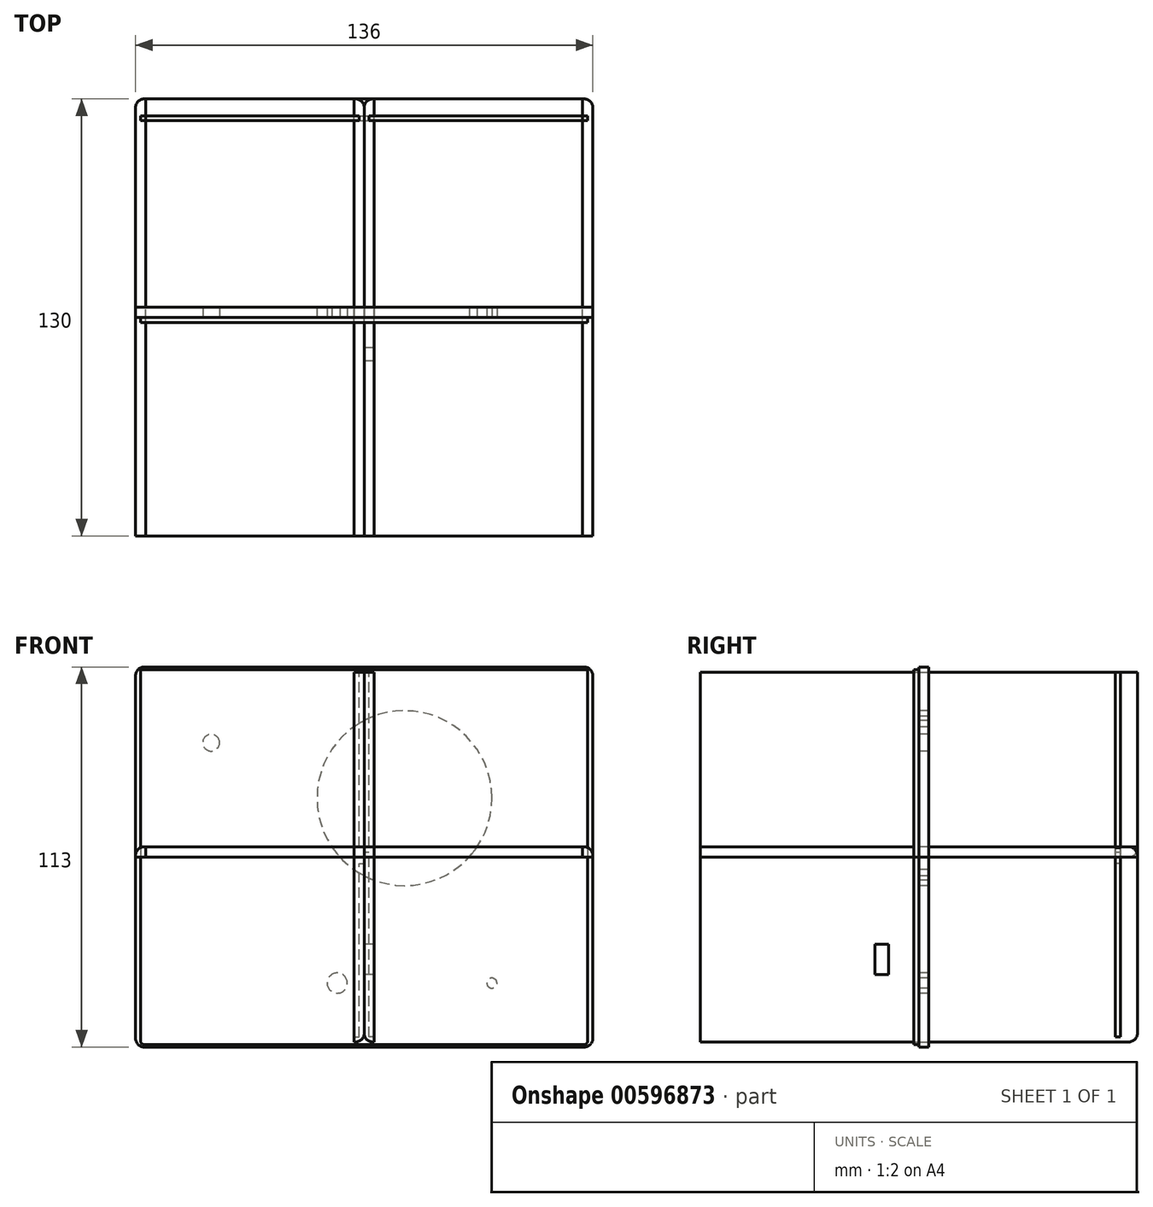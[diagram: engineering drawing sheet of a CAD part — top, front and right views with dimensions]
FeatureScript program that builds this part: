
annotation { "Feature Type Name" : "Feature", "Feature Type Description" : "" }
export const myFeature = defineFeature(function(context is Context, id is Id, definition is map)
    precondition{}
    {
        {
            var Q0;
            Q0=qCreatedBy(makeId("Right.planeOp"),FACE);
            var sketch = newSketch(context, id + "F0", { "sketchPlane" : qUnion([Q0])});
            skLineSegment(sketch, "E0.bottom", {"start": v(-65, 55) * mm, "end": v(65, 55) * mm});
            skLineSegment(sketch, "E0.top", {"start": v(-65, -55) * mm, "end": v(65, -55) * mm});
            skLineSegment(sketch, "E0.left", {"start": v(-65, 55) * mm, "end": v(-65, -55) * mm});
            skLineSegment(sketch, "E0.right", {"start": v(65, 55) * mm, "end": v(65, -55) * mm});
            skPoint(sketch, "E0.middle", {"position": v(0, 0) * mm});
            skSolve(sketch);
        }
        {
            var Q0;
            Q0 = qSketchRegion(id + "F0", true);
            extrude(context, id + "F1", {"entities" : qUnion([Q0]), "oppositeDirection" : true, "depth" : 3 * mm, "offsetDistance" : 25.4 * mm});
        }
        {
            var Q0;
            Q0=makeQuery(id+"F1.opExtrude","SWEPT_FACE",FACE,{"disambiguationData":[OSD([sQuery(id+"F0.wireOp",EDGE,"E0.bottom")])]});
            var sketch = newSketch(context, id + "F2", { "sketchPlane" : qUnion([Q0])});
            skLineSegment(sketch, "E1.bottom", {"start": v(-3, 60) * mm, "end": v(-1.5, 60) * mm});
            skLineSegment(sketch, "E1.top", {"start": v(-3, 58.5) * mm, "end": v(-1.5, 58.5) * mm});
            skLineSegment(sketch, "E1.left", {"start": v(-3, 60) * mm, "end": v(-3, 58.5) * mm});
            skLineSegment(sketch, "E1.right", {"start": v(-1.5, 60) * mm, "end": v(-1.5, 58.5) * mm});
            skSolve(sketch);
        }
        {
            var Q0;
            Q0 = qSketchRegion(id + "F2", true);
            extrude(context, id + "F3", {"entities" : qUnion([Q0]), "operationType" : NewBodyOperationType.REMOVE, "oppositeDirection" : true, "depth" : 108.5 * mm, "offsetDistance" : 25.4 * mm});
        }
        {
            var Q0;
            Q0=qCreatedBy(makeId("Top.planeOp"),FACE);
            var sketch = newSketch(context, id + "F4", { "sketchPlane" : qUnion([Q0])});
            skLineSegment(sketch, "E2.bottom", {"start": v(-68, 65) * mm, "end": v(68, 65) * mm});
            skLineSegment(sketch, "E2.top", {"start": v(-68, -65) * mm, "end": v(68, -65) * mm});
            skLineSegment(sketch, "E2.left", {"start": v(-68, 65) * mm, "end": v(-68, -65) * mm});
            skLineSegment(sketch, "E2.right", {"start": v(68, 65) * mm, "end": v(68, -65) * mm});
            skPoint(sketch, "E2.middle", {"position": v(0, 0) * mm});
            skSolve(sketch);
        }
        {
            var Q0;
            Q0 = qSketchRegion(id + "F4", true);
            extrude(context, id + "F5", {"entities" : qUnion([Q0]), "depth" : 3 * mm, "offsetDistance" : 25.4 * mm});
        }
        {
            var Q0;
            Q0=makeQuery(id+"F5.opExtrude","CAP_FACE",FACE,{"disambiguationData":[OSD([sQuery(id+"F4.wireOp",EDGE,"E2.bottom"),sQuery(id+"F4.wireOp",EDGE,"E2.top"),sQuery(id+"F4.wireOp",EDGE,"E2.left"),sQuery(id+"F4.wireOp",EDGE,"E2.right")])],"isStart":false});
            var sketch = newSketch(context, id + "F6", { "sketchPlane" : qUnion([Q0])});
            skLineSegment(sketch, "E3.bottom", {"start": v(-66.5, 58.5) * mm, "end": v(66.5, 58.5) * mm});
            skLineSegment(sketch, "E3.top", {"start": v(-66.5, 60) * mm, "end": v(66.5, 60) * mm});
            skLineSegment(sketch, "E3.left", {"start": v(-66.5, 58.5) * mm, "end": v(-66.5, 60) * mm});
            skLineSegment(sketch, "E3.right", {"start": v(66.5, 58.5) * mm, "end": v(66.5, 60) * mm});
            skPoint(sketch, "E3.middle", {"position": v(0, 59.25) * mm});
            skSolve(sketch);
        }
        {
            var Q0;
            Q0=makeQuery(id+"F6.imprint","IMPRINT",FACE,{"disambiguationData":[TD([[makeQuery(id+"F6.imprint","IMPRINT",EDGE,{"derivedFrom":sQuery(id+"F6.wireOp",EDGE,"E3.bottom")}),1.0]])]});
            var Q1;
            Q1 = qSketchRegion(id + "F6", true);
            extrude(context, id + "F7", {"entities" : qUnion([Q0, Q1]), "operationType" : NewBodyOperationType.REMOVE, "oppositeDirection" : true, "depth" : 5 * mm, "offsetDistance" : 25.4 * mm});
        }
        {
            var Q0;
            Q0=qCreatedBy(makeId("Front.planeOp"),FACE);
            var sketch = newSketch(context, id + "F8", { "sketchPlane" : qUnion([Q0])});
            skLineSegment(sketch, "E4.bottom", {"start": v(66.5, 55.75) * mm, "end": v(-66.5, 55.75) * mm});
            skLineSegment(sketch, "E4.top", {"start": v(66.5, -55.75) * mm, "end": v(-66.5, -55.75) * mm});
            skLineSegment(sketch, "E4.left", {"start": v(66.5, 55.75) * mm, "end": v(66.5, -55.75) * mm});
            skLineSegment(sketch, "E4.right", {"start": v(-66.5, 55.75) * mm, "end": v(-66.5, -55.75) * mm});
            skPoint(sketch, "E4.middle", {"position": v(0, 0) * mm});
            skSolve(sketch);
        }
        {
            var Q0;
            Q0 = qSketchRegion(id + "F8", true);
            extrude(context, id + "F9", {"entities" : qUnion([Q0]), "depth" : 1.5 * mm, "offsetDistance" : 25.4 * mm});
        }
        {
            var Q0;
            Q0 = qSketchRegion(id + "F0", true);
            extrude(context, id + "F10", {"entities" : qUnion([Q0]), "depth" : 3 * mm, "offsetDistance" : 25.4 * mm});
        }
        {
            var Q0;
            Q0=makeQuery(id+"F10.opExtrude","SWEPT_FACE",FACE,{"disambiguationData":[OSD([sQuery(id+"F0.wireOp",EDGE,"E0.bottom")])]});
            var sketch = newSketch(context, id + "F11", { "sketchPlane" : qUnion([Q0])});
            skLineSegment(sketch, "E5.bottom", {"start": v(3, 60) * mm, "end": v(1.5, 60) * mm});
            skLineSegment(sketch, "E5.top", {"start": v(3, 58.5) * mm, "end": v(1.5, 58.5) * mm});
            skLineSegment(sketch, "E5.left", {"start": v(3, 60) * mm, "end": v(3, 58.5) * mm});
            skLineSegment(sketch, "E5.right", {"start": v(1.5, 60) * mm, "end": v(1.5, 58.5) * mm});
            skSolve(sketch);
        }
        {
            var Q0;
            Q0 = qSketchRegion(id + "F11", true);
            extrude(context, id + "F12", {"entities" : qUnion([Q0]), "operationType" : NewBodyOperationType.REMOVE, "oppositeDirection" : true, "depth" : 108.5 * mm, "offsetDistance" : 25.4 * mm});
        }
        {
            var Q0;
            Q0=qCreatedBy(makeId("Top.planeOp"),FACE);
            var sketch = newSketch(context, id + "F13", { "sketchPlane" : qUnion([Q0])});
            skLineSegment(sketch, "E6.bottom", {"start": v(-65, -65) * mm, "end": v(65, -65) * mm});
            skLineSegment(sketch, "E6.top", {"start": v(-65, 65) * mm, "end": v(65, 65) * mm});
            skLineSegment(sketch, "E6.left", {"start": v(-65, -65) * mm, "end": v(-65, 65) * mm});
            skLineSegment(sketch, "E6.right", {"start": v(65, -65) * mm, "end": v(65, 65) * mm});
            skPoint(sketch, "E6.middle", {"position": v(0, 0) * mm});
            skSolve(sketch);
        }
        {
            var Q0;
            Q0 = qSketchRegion(id + "F13", true);
            extrude(context, id + "F14", {"entities" : qUnion([Q0]), "depth" : 3 * mm, "offsetDistance" : 25.4 * mm});
        }
        {
            var Q0;
            Q0=makeQuery(id+"F10.opExtrude","CAP_FACE",FACE,{"disambiguationData":[OSD([sQuery(id+"F0.wireOp",EDGE,"E0.bottom"),sQuery(id+"F0.wireOp",EDGE,"E0.top"),sQuery(id+"F0.wireOp",EDGE,"E0.left"),sQuery(id+"F0.wireOp",EDGE,"E0.right")])],"isStart":true});
            var sketch = newSketch(context, id + "F15", { "sketchPlane" : qUnion([Q0])});
            skLineSegment(sketch, "E7.bottom", {"start": v(9, -26) * mm, "end": v(13, -26) * mm});
            skLineSegment(sketch, "E7.top", {"start": v(9, -35) * mm, "end": v(13, -35) * mm});
            skLineSegment(sketch, "E7.left", {"start": v(9, -26) * mm, "end": v(9, -35) * mm});
            skLineSegment(sketch, "E7.right", {"start": v(13, -26) * mm, "end": v(13, -35) * mm});
            skSolve(sketch);
        }
        {
            var Q0;
            Q0 = qSketchRegion(id + "F15", true);
            extrude(context, id + "F16", {"entities" : qUnion([Q0]), "operationType" : NewBodyOperationType.REMOVE, "oppositeDirection" : true, "depth" : 3 * mm, "offsetDistance" : 25.4 * mm});
        }
        {
            var Q0;
            Q0=makeQuery(id+"F10.opExtrude","CAP_EDGE",EDGE,{"disambiguationData":[OSD([sQuery(id+"F0.wireOp",EDGE,"E0.top")])],"isStart":true});
            var Q1;
            Q1=makeQuery(id+"F5.opExtrude","CAP_EDGE",EDGE,{"disambiguationData":[OSD([sQuery(id+"F4.wireOp",EDGE,"E2.bottom")])],"isStart":false});
            fillet(context, id + "F17", {"entities" : qUnion([Q0, Q1]), "radius" : 2.54 * mm, "tangentPropagation" : true, "allowEdgeOverflow" : false});
        }
        {
            var Q0;
            Q0=makeQuery(id+"F5.opExtrude","CAP_EDGE",EDGE,{"disambiguationData":[OSD([sQuery(id+"F4.wireOp",EDGE,"E2.left")])],"isStart":false});
            var Q1;
            Q1=makeQuery(id+"F5.opExtrude","CAP_EDGE",EDGE,{"disambiguationData":[OSD([sQuery(id+"F4.wireOp",EDGE,"E2.right")])],"isStart":false});
            var Q2;
            Q2=makeQuery(id+"F10.opExtrude","CAP_EDGE",EDGE,{"disambiguationData":[OSD([sQuery(id+"F0.wireOp",EDGE,"E0.right")])],"isStart":true});
            fillet(context, id + "F18", {"entities" : qUnion([Q0, Q1, Q2]), "radius" : 2.54 * mm, "tangentPropagation" : true, "allowEdgeOverflow" : false});
        }
        {
            var Q0;
            Q0=makeQuery(id+"F1.opExtrude","CAP_EDGE",EDGE,{"disambiguationData":[OSD([sQuery(id+"F0.wireOp",EDGE,"E0.top")])],"isStart":true});
            var Q1;
            Q1=makeQuery(id+"F1.opExtrude","SWEPT_EDGE",EDGE,{"disambiguationData":[OSD([sQuery(id+"F0.wireOp",EDGE,"E0.top"),sQuery(id+"F0.wireOp",EDGE,"E0.right")])]});
            var Q2;
            Q2=makeQuery(id+"F1.opExtrude","CAP_EDGE",EDGE,{"disambiguationData":[OSD([sQuery(id+"F0.wireOp",EDGE,"E0.right")])],"isStart":true});
            fillet(context, id + "F19", {"entities" : qUnion([Q0, Q1, Q2]), "radius" : 2.54 * mm, "tangentPropagation" : true, "allowEdgeOverflow" : false});
        }
        {
            var Q0;
            Q0=makeQuery(id+"F14.opExtrude","CAP_EDGE",EDGE,{"disambiguationData":[OSD([sQuery(id+"F13.wireOp",EDGE,"E6.top")])],"isStart":true});
            fillet(context, id + "F20", {"entities" : qUnion([Q0]), "radius" : 2.54 * mm, "tangentPropagation" : true, "allowEdgeOverflow" : false});
        }
        {
            var Q0;
            Q0=makeQuery(id+"F9.opExtrude","SWEPT_EDGE",EDGE,{"disambiguationData":[OSD([sQuery(id+"F8.wireOp",EDGE,"E4.top"),sQuery(id+"F8.wireOp",EDGE,"E4.left")])]});
            var Q1;
            Q1=makeQuery(id+"F9.opExtrude","SWEPT_EDGE",EDGE,{"disambiguationData":[OSD([sQuery(id+"F8.wireOp",EDGE,"E4.top"),sQuery(id+"F8.wireOp",EDGE,"E4.right")])]});
            fillet(context, id + "F21", {"entities" : qUnion([Q0, Q1]), "radius" : 1.02 * mm, "tangentPropagation" : true, "allowEdgeOverflow" : false});
        }
        {
            var Q0;
            Q0=qCreatedBy(makeId("Front.planeOp"),FACE);
            var sketch = newSketch(context, id + "F22", { "sketchPlane" : qUnion([Q0])});
            skLineSegment(sketch, "E8.bottom", {"start": v(-68, 56.5) * mm, "end": v(68, 56.5) * mm});
            skLineSegment(sketch, "E8.top", {"start": v(-68, -56.5) * mm, "end": v(68, -56.5) * mm});
            skLineSegment(sketch, "E8.left", {"start": v(-68, 56.5) * mm, "end": v(-68, -56.5) * mm});
            skLineSegment(sketch, "E8.right", {"start": v(68, 56.5) * mm, "end": v(68, -56.5) * mm});
            skPoint(sketch, "E8.middle", {"position": v(0, 0) * mm});
            skSolve(sketch);
        }
        {
            var Q0;
            Q0 = qSketchRegion(id + "F22", true);
            extrude(context, id + "F23", {"entities" : qUnion([Q0]), "oppositeDirection" : true, "depth" : 3 * mm, "offsetDistance" : 25.4 * mm});
        }
        {
            var Q0;
            Q0=makeQuery(id+"F23.opExtrude","SWEPT_EDGE",EDGE,{"disambiguationData":[OSD([sQuery(id+"F22.wireOp",EDGE,"E8.bottom"),sQuery(id+"F22.wireOp",EDGE,"E8.left")])]});
            var Q1;
            Q1=makeQuery(id+"F23.opExtrude","SWEPT_EDGE",EDGE,{"disambiguationData":[OSD([sQuery(id+"F22.wireOp",EDGE,"E8.bottom"),sQuery(id+"F22.wireOp",EDGE,"E8.right")])]});
            var Q2;
            Q2=makeQuery(id+"F23.opExtrude","SWEPT_EDGE",EDGE,{"disambiguationData":[OSD([sQuery(id+"F22.wireOp",EDGE,"E8.top"),sQuery(id+"F22.wireOp",EDGE,"E8.right")])]});
            var Q3;
            Q3=makeQuery(id+"F23.opExtrude","SWEPT_EDGE",EDGE,{"disambiguationData":[OSD([sQuery(id+"F22.wireOp",EDGE,"E8.top"),sQuery(id+"F22.wireOp",EDGE,"E8.left")])]});
            fillet(context, id + "F24", {"entities" : qUnion([Q0, Q1, Q2, Q3]), "radius" : 2.54 * mm, "tangentPropagation" : true, "allowEdgeOverflow" : false});
        }
        {
            var Q0;
            Q0=makeQuery(id+"F23.opExtrude","CAP_FACE",FACE,{"disambiguationData":[OSD([sQuery(id+"F22.wireOp",EDGE,"E8.bottom"),sQuery(id+"F22.wireOp",EDGE,"E8.top"),sQuery(id+"F22.wireOp",EDGE,"E8.left"),sQuery(id+"F22.wireOp",EDGE,"E8.right")])],"isStart":true});
            var sketch = newSketch(context, id + "F25", { "sketchPlane" : qUnion([Q0])});
            skCircle(sketch, "E9", {"center": v(12, 17.5) * mm, "radius": 26 * mm});
            skCircle(sketch, "E10", {"center": v(-45.5, 34) * mm, "radius": 2.5 * mm});
            skCircle(sketch, "E11", {"center": v(-8, -37.5) * mm, "radius": 3 * mm});
            skCircle(sketch, "E12", {"center": v(38, -37.5) * mm, "radius": 1.5 * mm});
            skLineSegment(sketch, "E13", {"start": v(-8, -37.5) * mm, "end": v(38, -37.5) * mm});
            skSolve(sketch);
        }
        {
            var Q0;
            Q0 = qSketchRegion(id + "F25", true);
            extrude(context, id + "F26", {"entities" : qUnion([Q0]), "operationType" : NewBodyOperationType.REMOVE, "oppositeDirection" : true, "depth" : 3 * mm, "offsetDistance" : 25.4 * mm});
        }
        {
            var Q0;
            Q0=makeQuery(id+"F14.opExtrude","SWEPT_FACE",FACE,{"disambiguationData":[OSD([sQuery(id+"F13.wireOp",EDGE,"E6.right")])]});
            var sketch = newSketch(context, id + "F27", { "sketchPlane" : qUnion([Q0])});
            skLineSegment(sketch, "E14.bottom", {"start": v(58.5, 3) * mm, "end": v(60, 3) * mm});
            skLineSegment(sketch, "E14.top", {"start": v(58.5, 1.5) * mm, "end": v(60, 1.5) * mm});
            skLineSegment(sketch, "E14.left", {"start": v(58.5, 3) * mm, "end": v(58.5, 1.5) * mm});
            skLineSegment(sketch, "E14.right", {"start": v(60, 3) * mm, "end": v(60, 1.5) * mm});
            skSolve(sketch);
        }
        {
            var Q0;
            Q0=makeQuery(id+"F27.imprint","IMPRINT",FACE,{"disambiguationData":[TD([[makeQuery(id+"F27.imprint","IMPRINT",EDGE,{"derivedFrom":sQuery(id+"F27.wireOp",EDGE,"E14.bottom")}),-1.0]])]});
            extrude(context, id + "F28", {"entities" : qUnion([Q0]), "operationType" : NewBodyOperationType.REMOVE, "oppositeDirection" : true, "depth" : 130 * mm, "offsetDistance" : 25.4 * mm});
        }
    });
